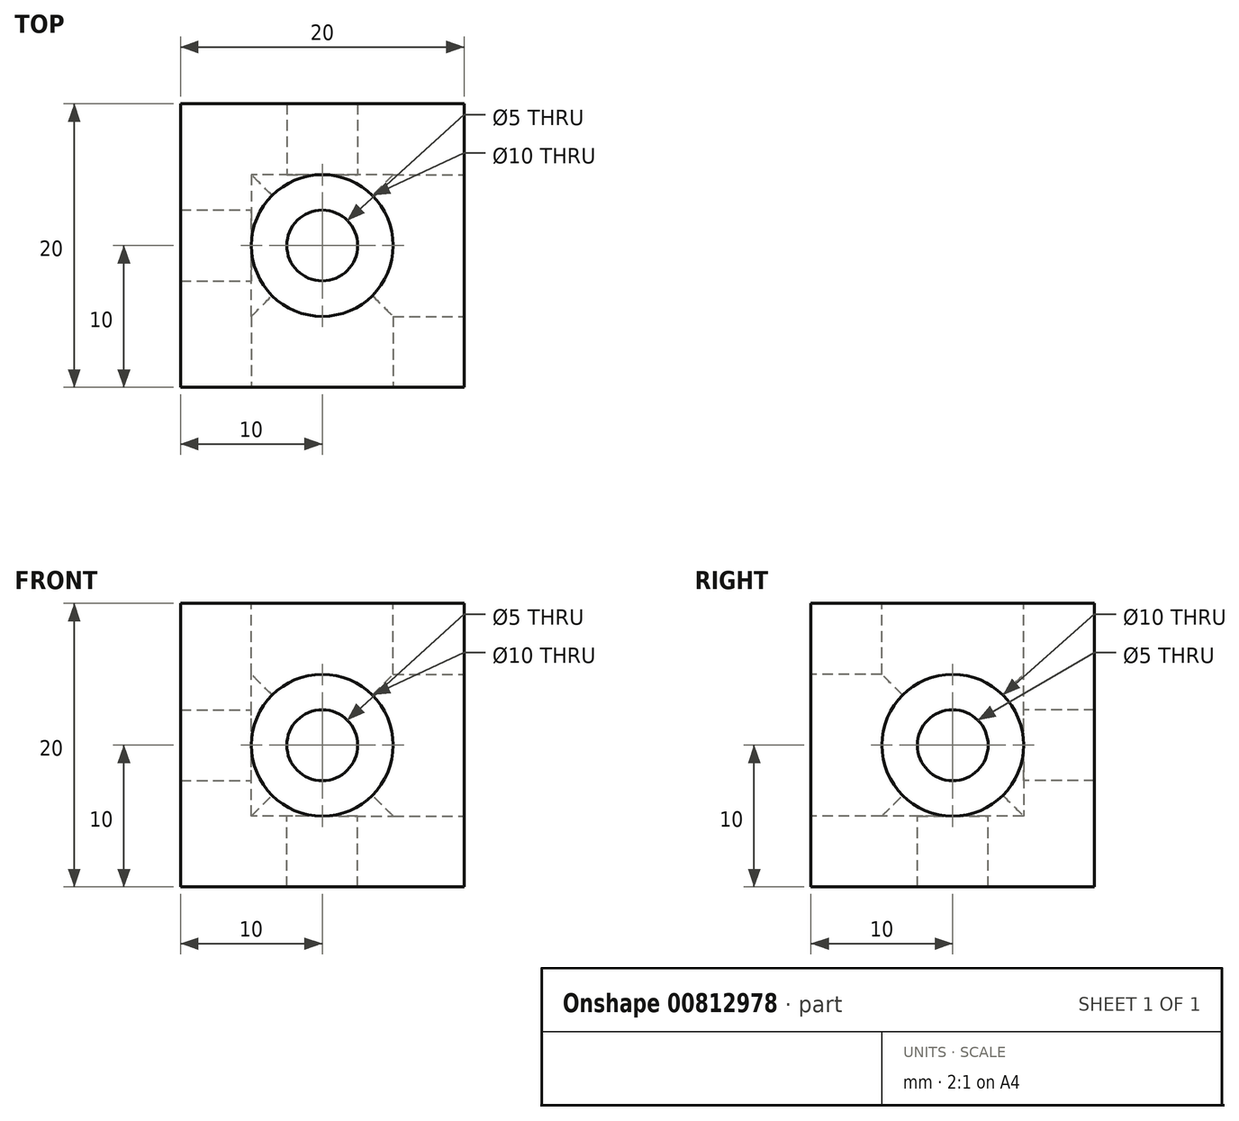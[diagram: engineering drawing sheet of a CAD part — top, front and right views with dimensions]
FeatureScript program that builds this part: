
annotation { "Feature Type Name" : "Feature", "Feature Type Description" : "" }
export const myFeature = defineFeature(function(context is Context, id is Id, definition is map)
    precondition{}
    {
        {
            var Q0;
            Q0=qCreatedBy(makeId("Top.planeOp"),FACE);
            var sketch = newSketch(context, id + "F0", { "sketchPlane" : qUnion([Q0])});
            skLineSegment(sketch, "E0.bottom", {"start": v(10, -10) * mm, "end": v(-10, -10) * mm});
            skLineSegment(sketch, "E0.top", {"start": v(10, 10) * mm, "end": v(-10, 10) * mm});
            skLineSegment(sketch, "E0.left", {"start": v(10, -10) * mm, "end": v(10, 10) * mm});
            skLineSegment(sketch, "E0.right", {"start": v(-10, -10) * mm, "end": v(-10, 10) * mm});
            skPoint(sketch, "E0.middle", {"position": v(0, 0) * mm});
            skSolve(sketch);
        }
        {
            var Q0;
            Q0=qSketchRegion(id+"F0",true);
            extrude(context, id + "F1", {"entities" : qUnion([Q0]), "depth" : 20 * mm, "offsetDistance" : 25 * mm});
        }
        {
            var Q0;
            Q0=makeQuery(id+"F1.opExtrude","SWEPT_FACE",FACE,{"disambiguationData":[OSD([sQuery(id+"F0.wireOp",EDGE,"E0.bottom")])]});
            var sketch = newSketch(context, id + "F2", { "sketchPlane" : qUnion([Q0])});
            skPoint(sketch, "E1", {"position": v(0, 10) * mm});
            skPoint(sketch, "E1.positionSnap0", {"position": v(10, 10) * mm});
            skSolve(sketch);
        }
        {
            var Q0;
            Q0=makeQuery(id+"F1.opExtrude","SWEPT_FACE",FACE,{"disambiguationData":[OSD([sQuery(id+"F0.wireOp",EDGE,"E0.left")])]});
            var sketch = newSketch(context, id + "F3", { "sketchPlane" : qUnion([Q0])});
            skPoint(sketch, "E2", {"position": v(0, 10) * mm});
            skPoint(sketch, "E2.positionSnap0", {"position": v(-10, 10) * mm});
            skSolve(sketch);
        }
        {
            var Q0;
            Q0=makeQuery(id+"F1.opExtrude","CAP_FACE",FACE,{"disambiguationData":[OSD([sQuery(id+"F0.wireOp",EDGE,"E0.bottom"),sQuery(id+"F0.wireOp",EDGE,"E0.top"),sQuery(id+"F0.wireOp",EDGE,"E0.left"),sQuery(id+"F0.wireOp",EDGE,"E0.right")])],"isStart":false});
            var sketch = newSketch(context, id + "F4", { "sketchPlane" : qUnion([Q0])});
            skPoint(sketch, "E3", {"position": v(0, 0) * mm});
            skSolve(sketch);
        }
        {
            var Q0;
            Q0=sQuery(id+"F2.wireOp",VERTEX,"E1");
            var Q1;
            Q1=sQuery(id+"F3.wireOp",VERTEX,"E2");
            var Q2;
            Q2=sQuery(id+"F4.wireOp",VERTEX,"E3");
            var Q3;
            Q3=makeQuery(id+"F1.opExtrude","SWEPT_BODY",BODY,{"disambiguationData":[OSD([sQuery(id+"F0.wireOp",EDGE,"E0.bottom"),sQuery(id+"F0.wireOp",EDGE,"E0.top"),sQuery(id+"F0.wireOp",EDGE,"E0.left"),sQuery(id+"F0.wireOp",EDGE,"E0.right")])]});
            hole(context, id + "F5", {"style" : HoleStyle.C_BORE, "endStyle" : HoleEndStyle.THROUGH, "holeDiameter" : 5 * mm, "cBoreDiameter" : 10 * mm, "cBoreDepth" : 15 * mm, "majorDiameter" : 5 * mm, "isTappedThrough" : true, "tappedDepth" : 12 * mm, "tapClearance" : 3, "locations" : qUnion([Q0, Q1, Q2]), "scope" : qUnion([Q3])});
        }
    });
